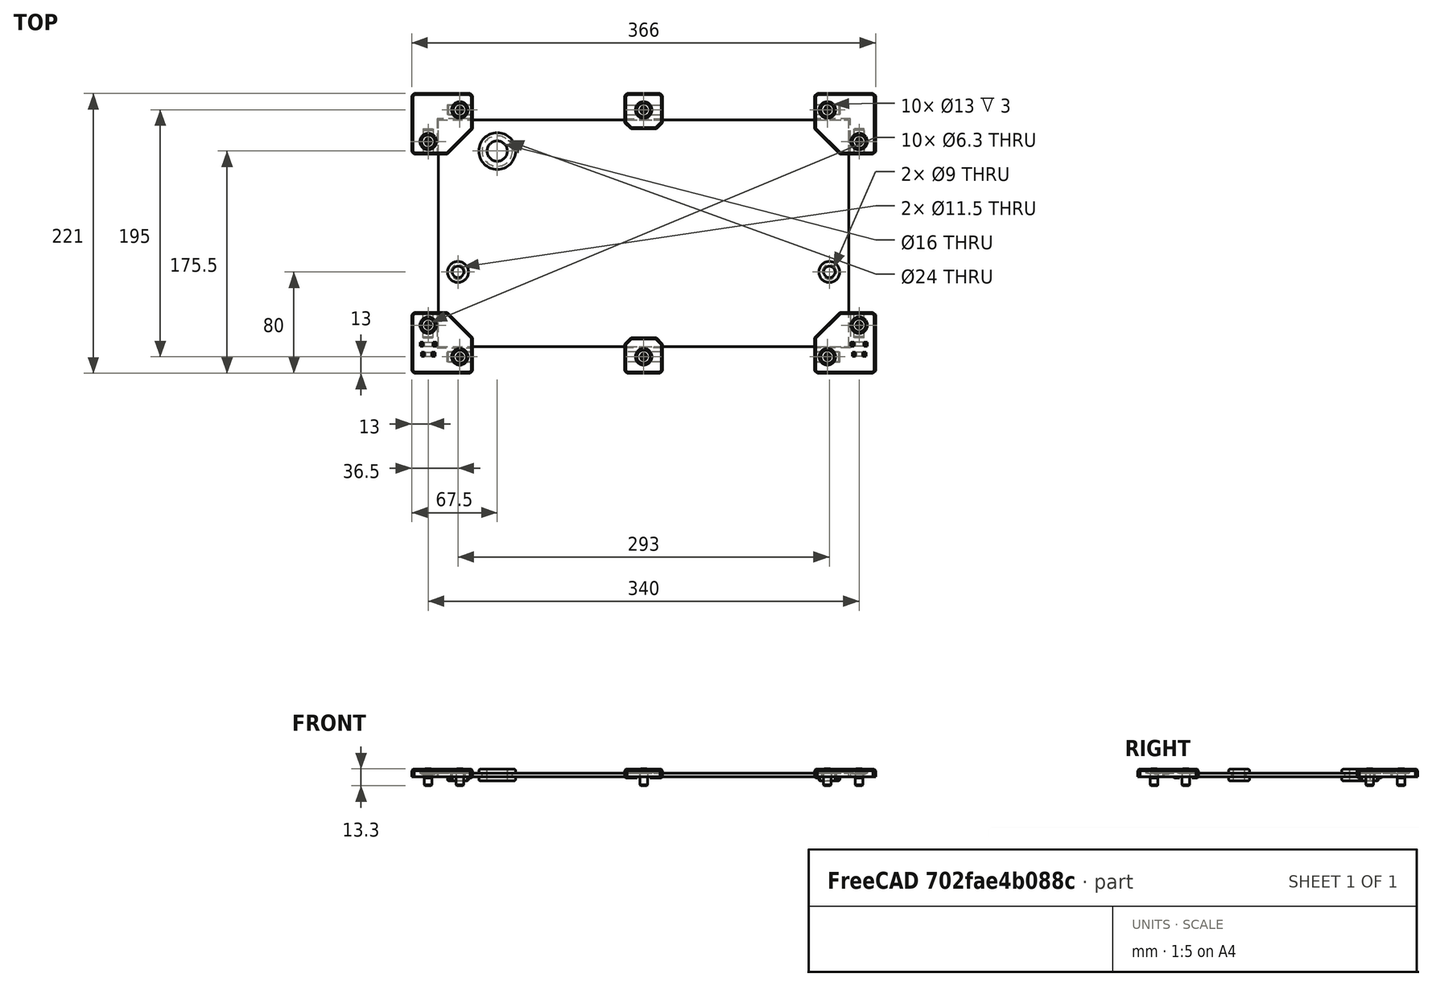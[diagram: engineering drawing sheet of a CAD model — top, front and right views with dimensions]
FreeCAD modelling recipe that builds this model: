
FCSTD DOCUMENT  (FreeCAD 0.19R24291 (Git))
Label: rear-top-panel-assembly
License: All rights reserved
LicenseURL: http://en.wikipedia.org/wiki/All_rights_reserved
objects: Part::FeaturePython×10, Part::Feature×10, PartDesign::CoordinateSystem×1, App::Part×1
note: 21 computed .brp shape members not serialized (recipe doc carries the construction recipe); baked Part::Feature solids carry a one-line shape summary decoded from their .brp

FEATURE [Part::FeaturePython] Screw048  label="M6x10-Screw021"  # Fasteners workbench fastener (typed FeaturePython)
  Placement = pos=(170,-47.5,3) rot=(0,0,1;0rad)
  diameter = 4
  invert = true
  length = 0
  lengthCustom = 10
  matchOuter = true
  offset = 0
  thread = false
  type = 39
FEATURE [Part::Feature] Fillet001002001003  label="cable-grommet-small002"
  Placement = pos=(-146.5,-5.5,-3) rot=(0,0,1;0rad)
  shape: bbox 17.86 x 17.86 x 9 mm, 14 faces (baked)
FEATURE [Part::FeaturePython] Screw051  label="M6x10-Screw029"  # Fasteners workbench fastener (typed FeaturePython)
  Placement = pos=(-4e-15,122.5,3) rot=(0,0,1;0rad)
  diameter = 4
  invert = true
  length = 0
  lengthCustom = 10
  matchOuter = true
  offset = 0
  thread = false
  type = 39
FEATURE [Part::FeaturePython] Screw049  label="M6x10-Screw031"  # Fasteners workbench fastener (typed FeaturePython)
  Placement = pos=(170,97.5,3) rot=(0,0,1;0rad)
  diameter = 4
  invert = true
  length = 0
  lengthCustom = 10
  matchOuter = true
  offset = 0
  thread = false
  type = 39
FEATURE [Part::Feature] Fillet001002001002  label="cable-grommet-small001"
  Placement = pos=(146.5,-5.5,-3) rot=(0,0,1;0rad)
  shape: bbox 17.86 x 17.86 x 9 mm, 14 faces (baked)
FEATURE [Part::FeaturePython] Screw046  label="M6x10-Screw024"  # Fasteners workbench fastener (typed FeaturePython)
  Placement = pos=(-170,-47.5,3) rot=(0,0,1;0rad)
  diameter = 4
  invert = true
  length = 0
  lengthCustom = 10
  matchOuter = true
  offset = 0
  thread = false
  type = 39
FEATURE [Part::FeaturePython] Screw047  label="M6x10-Screw022"  # Fasteners workbench fastener (typed FeaturePython)
  Placement = pos=(145,-72.5,3) rot=(0,0,1;0rad)
  diameter = 4
  invert = true
  length = 0
  lengthCustom = 10
  matchOuter = true
  offset = 0
  thread = false
  type = 39
FEATURE [Part::FeaturePython] Screw044  label="M6x10-Screw023"  # Fasteners workbench fastener (typed FeaturePython)
  Placement = pos=(-145,-72.5,3) rot=(0,0,1;0rad)
  diameter = 4
  invert = true
  length = 0
  lengthCustom = 10
  matchOuter = true
  offset = 0
  thread = false
  type = 39
FEATURE [PartDesign::CoordinateSystem] LCS_back_top_panel  label="LCS_back-top-panel"
  AttacherType = Attacher::AttachEngine3D
FEATURE [Part::FeaturePython] Screw045  label="M6x10-Screw020"  # Fasteners workbench fastener (typed FeaturePython)
  Placement = pos=(-7e-15,-72.5,3) rot=(0,0,1;0rad)
  diameter = 4
  invert = true
  length = 0
  lengthCustom = 10
  matchOuter = true
  offset = 0
  thread = false
  type = 39
FEATURE [Part::FeaturePython] Screw053  label="M6x10-Screw"  # Fasteners workbench fastener (typed FeaturePython)
  Placement = pos=(-145,122.5,3) rot=(0,0,1;0rad)
  diameter = 4
  invert = true
  length = 0
  lengthCustom = 10
  matchOuter = true
  offset = 0
  thread = false
  type = 39
FEATURE [Part::FeaturePython] Screw052  label="M6x10-Screw030"  # Fasteners workbench fastener (typed FeaturePython)
  Placement = pos=(-170,97.5,3) rot=(0,0,1;0rad)
  diameter = 4
  invert = true
  length = 0
  lengthCustom = 10
  matchOuter = true
  offset = 0
  thread = false
  type = 39
FEATURE [Part::FeaturePython] Screw050  label="M6x10-Screw032"  # Fasteners workbench fastener (typed FeaturePython)
  Placement = pos=(145,122.5,3) rot=(0,0,1;0rad)
  diameter = 4
  invert = true
  length = 0
  lengthCustom = 10
  matchOuter = true
  offset = 0
  thread = false
  type = 39
FEATURE [Part::Feature] Fillet001002001004  label="cable-grommet-big001"
  Placement = pos=(-115.5,90,-3) rot=(0,0,1;0rad)
  shape: bbox 31.39 x 31.39 x 9 mm, 14 faces (baked)
FEATURE [Part::Feature] Body001001001  label="top-corner-mount001"
  Placement = pos=(-155,107.5,-2.4e-14) rot=(0.57735,-0.57735,0.57735;4.18879rad)
  shape: bbox 48 x 48 x 7 mm, 47 faces (baked)
FEATURE [Part::Feature] Body002002002  label="top-corner-mount002"
  Placement = pos=(155,107.5,-2.4e-14) rot=(0,0.707107,-0.707107;3.14159rad)
  shape: bbox 48 x 48 x 7 mm, 47 faces (baked)
FEATURE [Part::Feature] Body002001001  label="side-mount001"
  Placement = pos=(15,-57.5,6) rot=(0.57735,0.57735,-0.57735;4.18879rad)
  shape: bbox 30 x 28 x 7 mm, 33 faces (baked)
FEATURE [Part::Feature] Body002002003  label="side-mount002"
  Placement = pos=(-15,107.5,6) rot=(0.57735,-0.57735,0.57735;4.18879rad)
  shape: bbox 30 x 28 x 7 mm, 33 faces (baked)
FEATURE [Part::Feature] Part__Mirroring002  label="bottom-left-corner-mount"
  Placement = pos=(-170,-43,0) rot=(0,0,1;3.14159rad)
  shape: bbox 48 x 48 x 7 mm, 83 faces (baked)
FEATURE [Part::Feature] Body002002001  label="bottom-right-corner-mount"
  Placement = pos=(170,-43,0) rot=(0,0,1;3.14159rad)
  shape: bbox 48 x 48 x 7 mm, 83 faces (baked)
FEATURE [Part::Feature] Cut008004003004014002002005003004003002003001003001002001002002011001006001001001  label="panel-324x179x3mm"
  shape: bbox 324 x 179 x 3 mm, 9 faces (baked)
FEATURE [App::Part] Part004  label="rear-top-panel"
  Group = -> [Screw044,Screw046,Screw045,Screw048,Screw047,Screw050,Screw049,Screw051,Screw053,Screw052,Fillet001002001002,Fillet001002001003,Fillet001002001004,LCS_back_top_panel,Body001001001,Body002002002,Body002001001,Body002002003,Part__Mirroring002,Body002002001,Cut008004003004014002002005003004003002003001003001002001002002011001006001001001]
  Origin = -> Origin004
